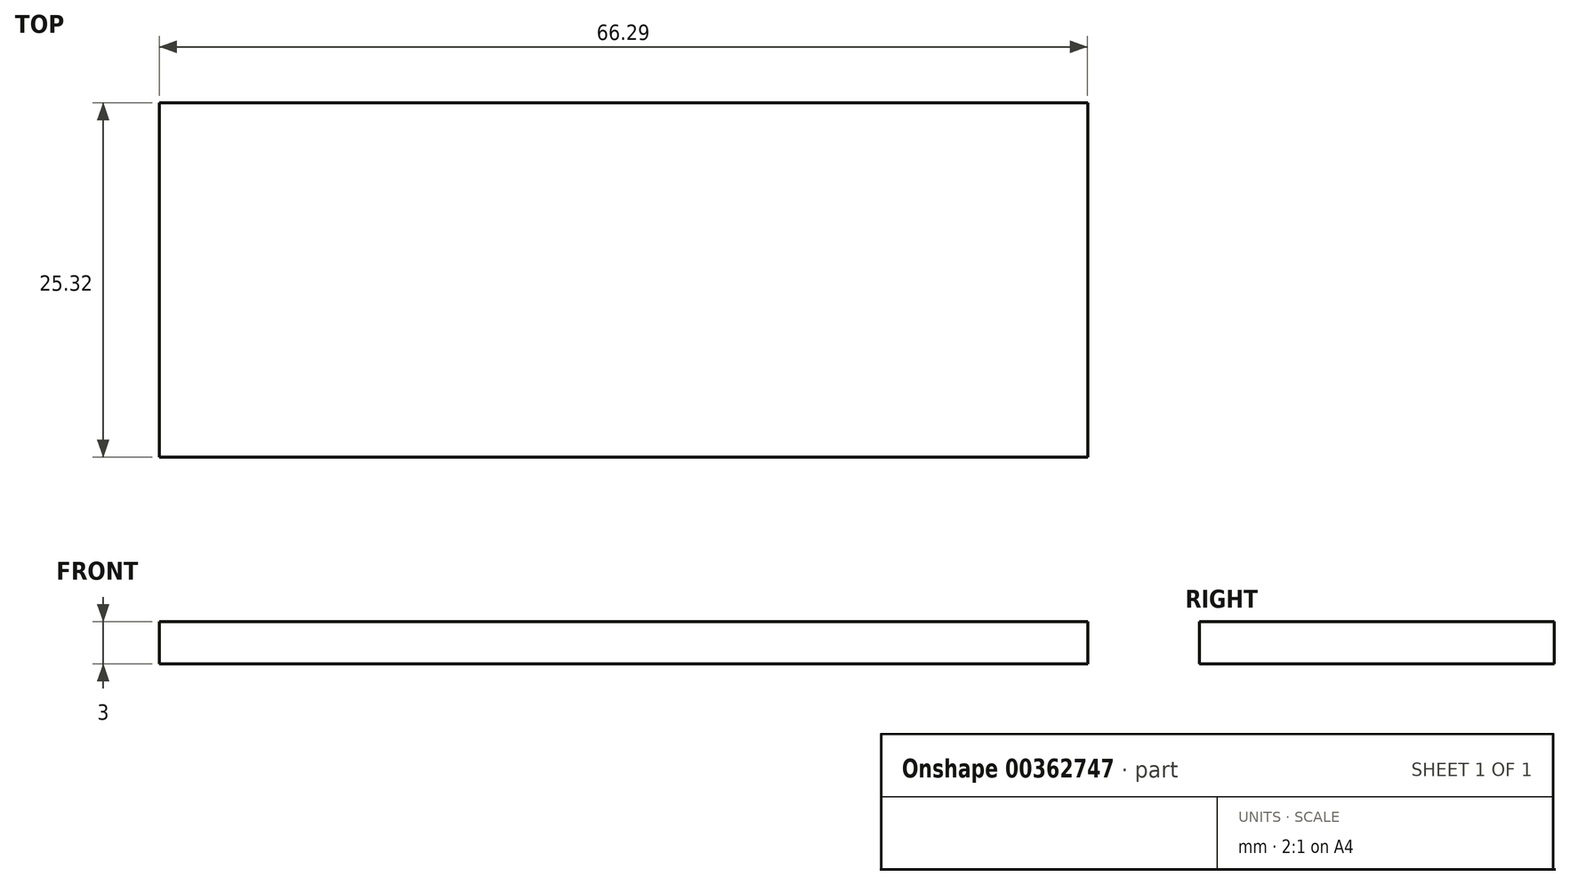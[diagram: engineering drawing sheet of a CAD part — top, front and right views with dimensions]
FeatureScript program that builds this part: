
annotation { "Feature Type Name" : "Feature", "Feature Type Description" : "" }
export const myFeature = defineFeature(function(context is Context, id is Id, definition is map)
    precondition{}
    {
        {
            var Q0;
            Q0=qCreatedBy(makeId("Top.planeOp"),FACE);
            var sketch = newSketch(context, id + "F0", { "sketchPlane" : qUnion([Q0])});
            skLineSegment(sketch, "E0.bottom", {"start": v(0, 0) * mm, "end": v(66.3, 0) * mm});
            skLineSegment(sketch, "E0.top", {"start": v(0, 25.32) * mm, "end": v(66.3, 25.32) * mm});
            skLineSegment(sketch, "E0.left", {"start": v(0, 0) * mm, "end": v(0, 25.32) * mm});
            skLineSegment(sketch, "E0.right", {"start": v(66.3, 0) * mm, "end": v(66.3, 25.32) * mm});
            skSolve(sketch);
        }
        {
            var Q0;
            Q0 = qSketchRegion(id + "F0", true);
            extrude(context, id + "F1", {"entities" : qUnion([Q0]), "depth" : 3 * mm});
        }
    });
